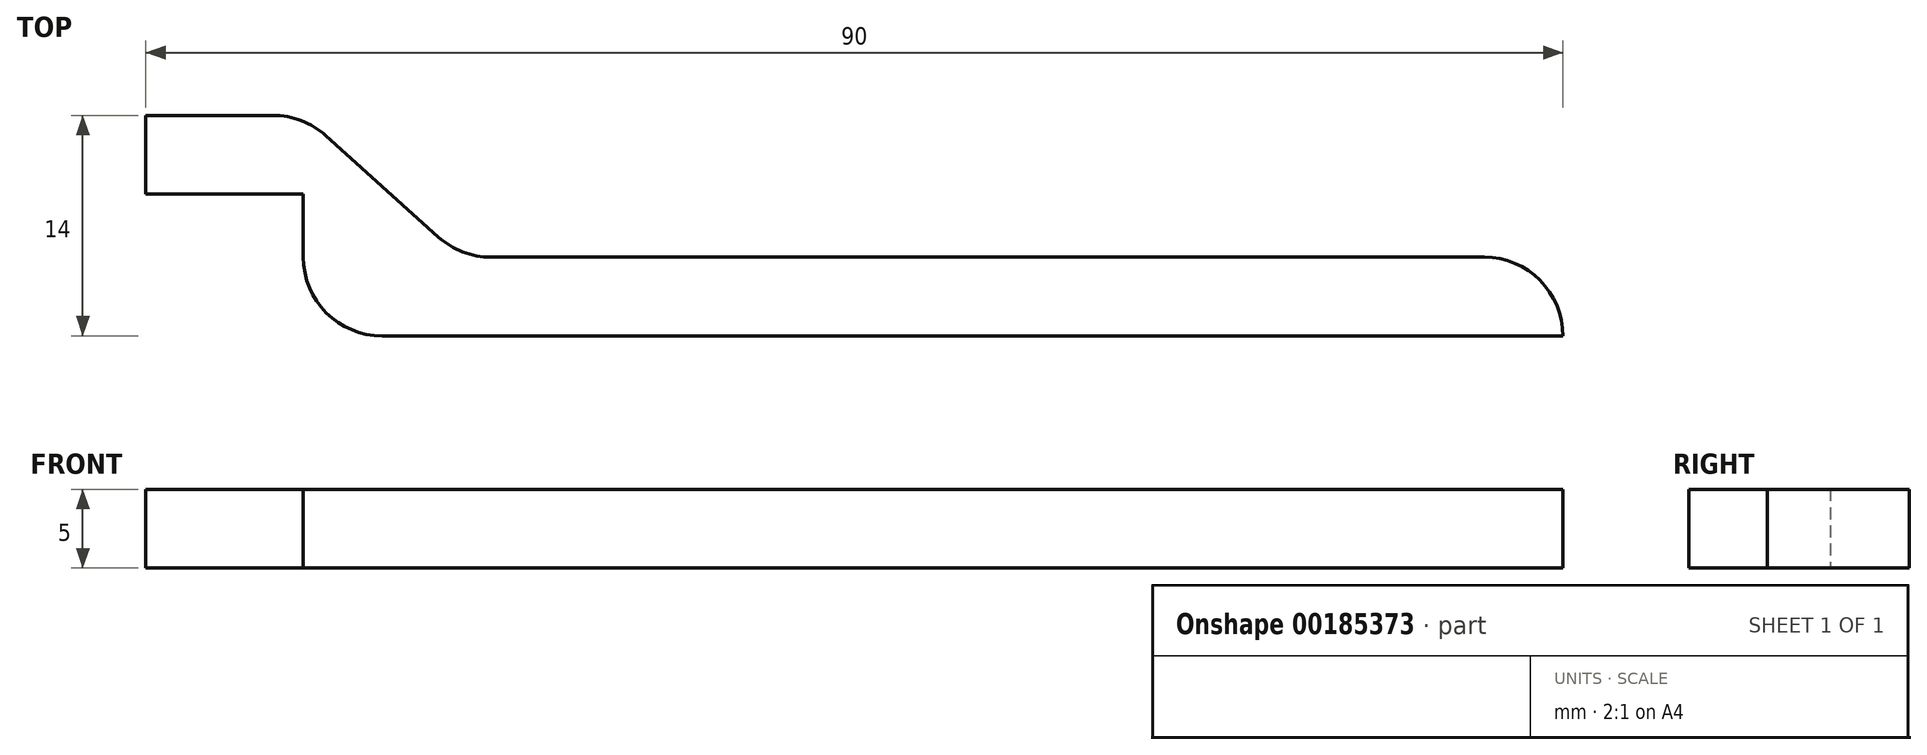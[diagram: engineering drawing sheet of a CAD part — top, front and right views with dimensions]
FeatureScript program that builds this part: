
annotation { "Feature Type Name" : "Feature", "Feature Type Description" : "" }
export const myFeature = defineFeature(function(context is Context, id is Id, definition is map)
    precondition{}
    {
        {
            var Q0;
            Q0=qCreatedBy(makeId("Top.planeOp"),FACE);
            var sketch = newSketch(context, id + "F0", { "sketchPlane" : qUnion([Q0])});
            skLineSegment(sketch, "E0", {"start": v(-20, 14) * mm, "end": v(-11.92, 14) * mm});
            skLineSegment(sketch, "E1", {"start": v(-8.57, 12.72) * mm, "end": v(-1.43, 6.28) * mm});
            skLineSegment(sketch, "E2", {"start": v(1.92, 5) * mm, "end": v(65, 5) * mm});
            skLineSegment(sketch, "E3", {"start": v(70, 0) * mm, "end": v(70, 0) * mm});
            skLineSegment(sketch, "E4", {"start": v(70, 0) * mm, "end": v(0, 0) * mm});
            skLineSegment(sketch, "E5", {"start": v(-10, 9) * mm, "end": v(-20, 9) * mm});
            skLineSegment(sketch, "E6", {"start": v(-20, 9) * mm, "end": v(-20, 14) * mm});
            skLineSegment(sketch, "E7", {"start": v(-10, 9) * mm, "end": v(-10, 5) * mm});
            skLineSegment(sketch, "E8", {"start": v(-5, 0) * mm, "end": v(0, 0) * mm});
            skPoint(sketch, "E9.visualSharp", {"position": v(-10, 0) * mm});
            skArc(sketch, "E9.filletArc", {"start": v(-10, 5) * mm, "mid": v(-8.54, 1.46) * mm, "end": v(-5, 0) * mm});
            skPoint(sketch, "E10.visualSharp", {"position": v(-10, 14) * mm});
            skArc(sketch, "E10.filletArc", {"start": v(-8.57, 12.72) * mm, "mid": v(-10.13, 13.67) * mm, "end": v(-11.92, 14) * mm});
            skPoint(sketch, "E11.visualSharp", {"position": v(0, 5) * mm});
            skArc(sketch, "E11.filletArc", {"start": v(-1.43, 6.28) * mm, "mid": v(0.13, 5.33) * mm, "end": v(1.92, 5) * mm});
            skPoint(sketch, "E12.visualSharp", {"position": v(70, 5) * mm});
            skArc(sketch, "E12.filletArc", {"start": v(70, 0) * mm, "mid": v(68.54, 3.54) * mm, "end": v(65, 5) * mm});
            skSolve(sketch);
        }
        {
            var Q0;
            Q0 = qSketchRegion(id + "F0", true);
            extrude(context, id + "F1", {"entities" : qUnion([Q0]), "depth" : 5 * mm});
        }
    });
